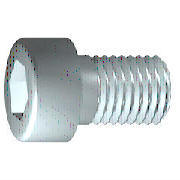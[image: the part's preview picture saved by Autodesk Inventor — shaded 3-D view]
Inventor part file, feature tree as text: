
AUTODESK INVENTOR PART (.ipt)
format: ipt  version: 2022 (Build 260153000, 153)  size: 196,608 bytes
history: native  units: mm (DEFAULTED — no unit token found)
features: sketch x2, extrude x1, plane x1, fillet x1
ambient origin geometry x7: Origin, YZ Plane, XY Plane, X Axis, Y Axis, Z Axis, Center Point
bodies: Solid1 (feature_tree), Body (feature_tree)
feature tree (5):
  extrude  "Slot"  Depth=3.0mm
  plane  "Work Plane1"
  fillet  "Fillet2"  Radius=3.0mm
  sketch  "Sketch1"  dims[d1=10.75mm d2=0.306825mm d3=3.0mm]
  sketch  "Sketch2"  dims[d4=1.3mm d5=60.0deg d6=3.0mm d7=3.0mm d8=2.886751mm d9=5.5mm d10=90.0deg d11=10.0mm d12=0.0mm d13=10.75mm d14=0.0mm d15=0.306725mm d16=0.306725mm d17=0.3mm d19=0.0mm d26=12.0mm d27=45.0deg d28=0.0mm d29=0.0mm d30=0.1mm]
